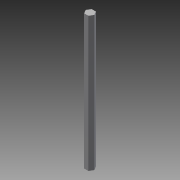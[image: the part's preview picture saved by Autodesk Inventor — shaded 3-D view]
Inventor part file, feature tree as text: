
AUTODESK INVENTOR PART (.ipt)
format: ipt  version: 2014 (Build 180170000, 170)  size: 73,728 bytes
history: native  units: in
note: dims shown in document units (in); Inventor stores cm internally (conversion verified against a paired STEP export)
features: extrude x1, sketch x1
ambient origin geometry x8: Origin, YZ Plane, XZ Plane, XY Plane, X Axis, Y Axis, Z Axis, Center Point
bodies: Solid1 (feature_tree)
feature tree (2):
  extrude  "Extrusion1"  Depth=9.0in TaperAngle=0.0deg
  sketch  "Sketch1"  dims[d0=0.5in d1=9.0in d2=0.0in]
